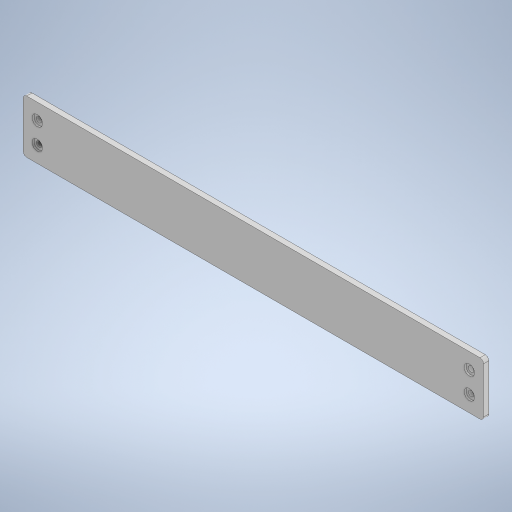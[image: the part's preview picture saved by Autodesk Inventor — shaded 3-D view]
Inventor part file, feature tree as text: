
AUTODESK INVENTOR PART (.ipt)
format: ipt  version: 2024.3 (Build 283343000, 343)  size: 271,360 bytes
history: native  units: mm
features: extrude x2, sketch x2, other x1, fillet x1, projected_geometry x1
ambient origin geometry x8: Origin, YZ Plane, XZ Plane, XY Plane, X Axis, Y Axis, Z Axis, Center Point
bodies: Body1 (feature_tree)
feature tree (7):
  other  "ソリッド1"
  extrude  "押し出し1"  Depth=260.0mm
  extrude  "押し出し2"  Depth=244.0mm
  fillet  "フィレット1"  Radius=8.0mm
  sketch  "スケッチ1"
  sketch  "スケッチ2"
  projected_geometry  "投影ループ1"
